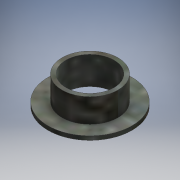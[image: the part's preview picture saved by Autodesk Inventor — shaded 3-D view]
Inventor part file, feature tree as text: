
AUTODESK INVENTOR PART (.ipt)
format: ipt  version: 2020.2 (Build 242310000, 310)  size: 119,808 bytes
history: native  units: mm
features: extrude x2, other x1, sketch x1
ambient origin geometry x8: Origin, YZ Plane, XZ Plane, XY Plane, X Axis, Y Axis, Z Axis, Center Point
bodies: Body1 (feature_tree)
feature tree (4):
  other  "ソリッド1"
  sketch  "スケッチ1"
  extrude  "押し出し1"  Depth=6.0mm
  extrude  "押し出し2"  Depth=7.0mm
